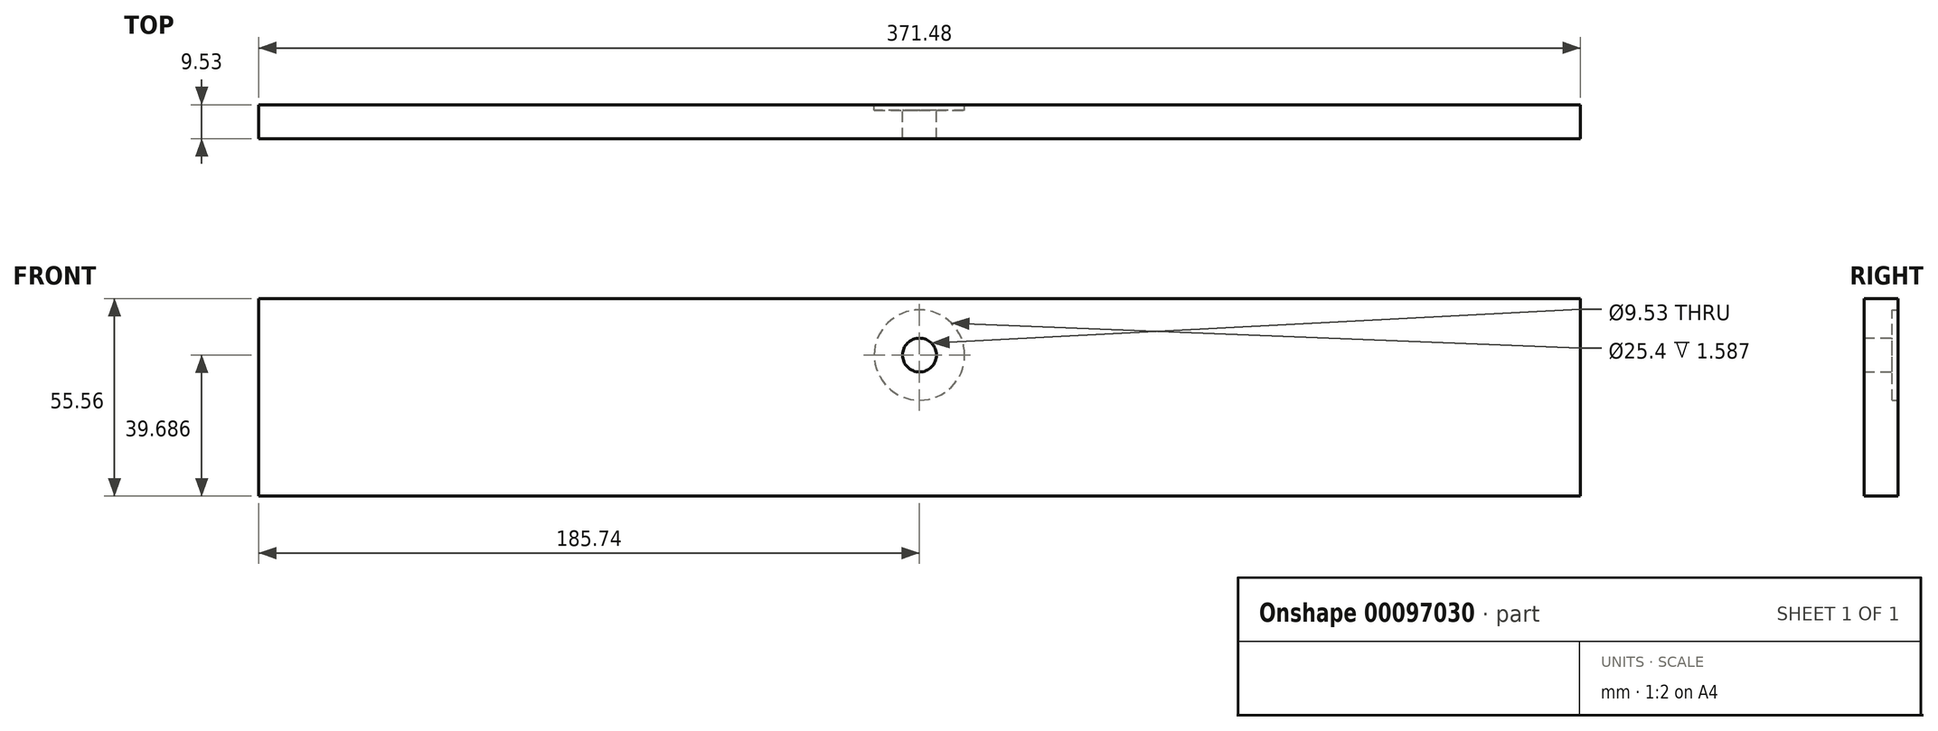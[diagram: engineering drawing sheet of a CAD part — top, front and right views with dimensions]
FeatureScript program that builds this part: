
annotation { "Feature Type Name" : "Feature", "Feature Type Description" : "" }
export const myFeature = defineFeature(function(context is Context, id is Id, definition is map)
    precondition{}
    {
        {
            var Q0;
            Q0=qCreatedBy(makeId("Front.planeOp"),FACE);
            var sketch = newSketch(context, id + "F0", { "sketchPlane" : qUnion([Q0])});
            skLineSegment(sketch, "E0.bottom", {"start": v(-185.74, 27.78) * mm, "end": v(185.74, 27.78) * mm});
            skLineSegment(sketch, "E0.top", {"start": v(-185.74, -27.78) * mm, "end": v(185.74, -27.78) * mm});
            skLineSegment(sketch, "E0.left", {"start": v(-185.74, 27.78) * mm, "end": v(-185.74, -27.78) * mm});
            skLineSegment(sketch, "E0.right", {"start": v(185.74, 27.78) * mm, "end": v(185.74, -27.78) * mm});
            skPoint(sketch, "E0.middle", {"position": v(0, 0) * mm});
            skCircle(sketch, "E1", {"center": v(0, 11.9) * mm, "radius": 3.18 * mm});
            skCircle(sketch, "E2.0", {"center": v(0, 11.9) * mm, "radius": 4.76 * mm});
            skCircle(sketch, "E3", {"center": v(0, 11.9) * mm, "radius": 12.7 * mm});
            skSolve(sketch);
        }
        {
            var Q0;
            Q0=makeQuery(id+"F0.imprint","IMPRINT",FACE,{"disambiguationData":[TD([[makeQuery(id+"F0.imprint","IMPRINT",EDGE,{"derivedFrom":sQuery(id+"F0.wireOp",EDGE,"E0.bottom")}),-1.0]])]});
            var Q1;
            Q1=makeQuery(id+"F0.imprint","IMPRINT",FACE,{"disambiguationData":[TD([[makeQuery(id+"F0.imprint","IMPRINT",EDGE,{"derivedFrom":sQuery(id+"F0.wireOp",EDGE,"E2.0")}),-1.0]])]});
            extrude(context, id + "F1", {"entities" : qUnion([Q0, Q1]), "depth" : 9.52 * mm});
        }
        {
            var Q0;
            Q0=makeQuery(id+"F0.imprint","IMPRINT",FACE,{"disambiguationData":[TD([[makeQuery(id+"F0.imprint","IMPRINT",EDGE,{"derivedFrom":sQuery(id+"F0.wireOp",EDGE,"E2.0")}),-1.0]])]});
            extrude(context, id + "F2", {"entities" : qUnion([Q0]), "operationType" : NewBodyOperationType.REMOVE, "depth" : 1.59 * mm});
        }
    });
